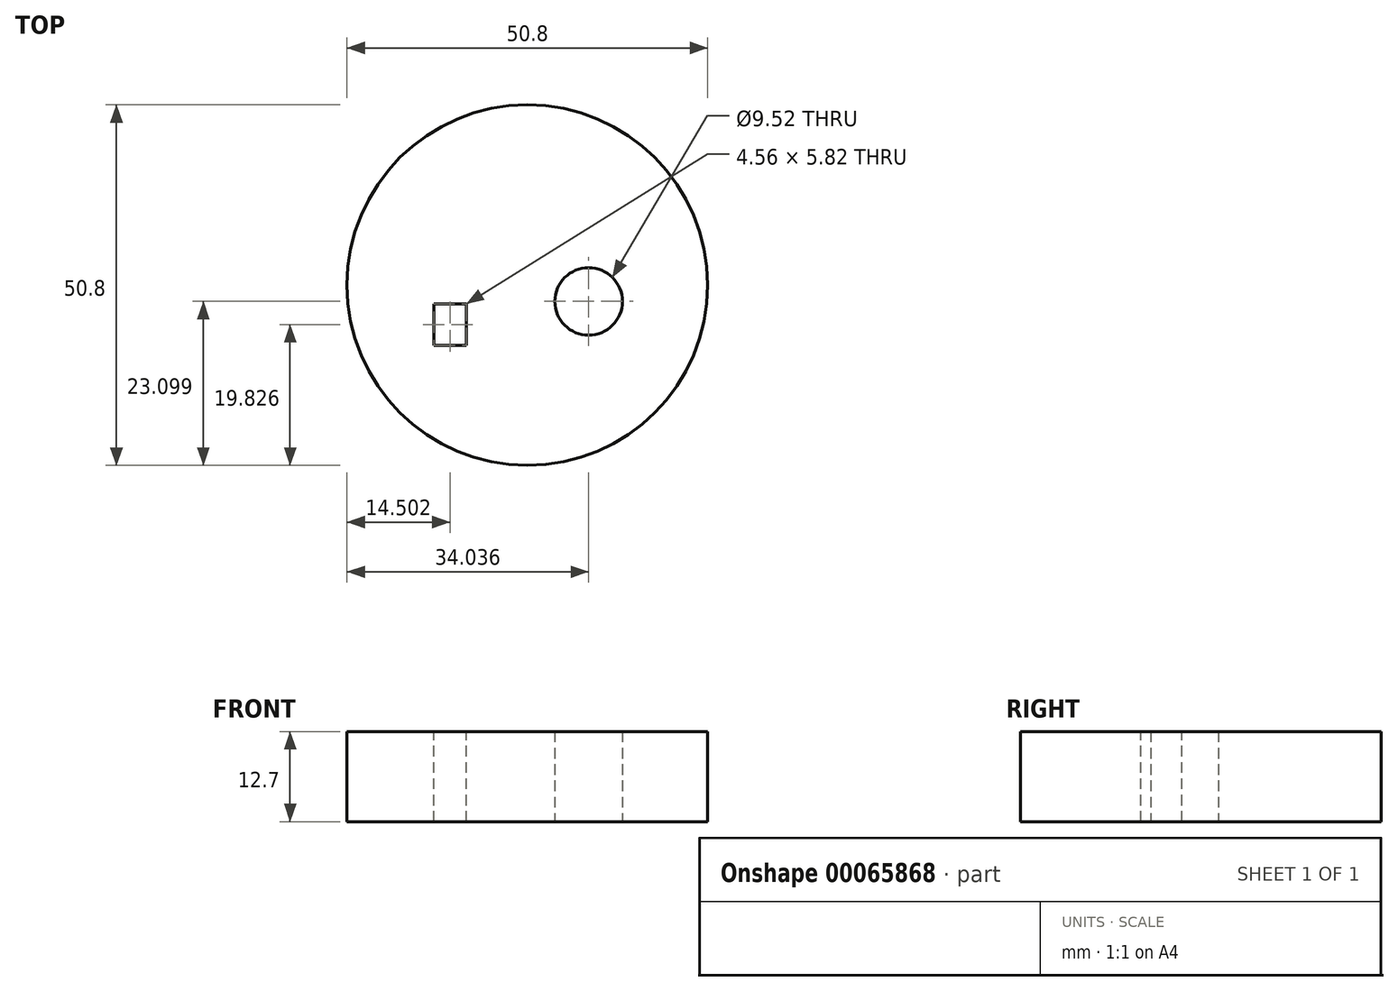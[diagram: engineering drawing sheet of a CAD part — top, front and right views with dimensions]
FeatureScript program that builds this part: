
annotation { "Feature Type Name" : "Feature", "Feature Type Description" : "" }
export const myFeature = defineFeature(function(context is Context, id is Id, definition is map)
    precondition{}
    {
        {
            var Q0;
            Q0=qCreatedBy(makeId("Top.planeOp"),FACE);
            var sketch = newSketch(context, id + "F0", { "sketchPlane" : qUnion([Q0])});
            skCircle(sketch, "E0", {"center": v(0, 0) * mm, "radius": 25.4 * mm});
            skSolve(sketch);
        }
        {
            var Q0;
            Q0 = qSketchRegion(id + "F0", true);
            extrude(context, id + "F1", {"entities" : qUnion([Q0]), "depth" : 12.7 * mm});
        }
        {
            var Q0;
            Q0=makeQuery(id+"F1.opExtrude","CAP_FACE",FACE,{"disambiguationData":[OSD([sQuery(id+"F0.wireOp",EDGE,"E0")])],"isStart":false});
            var sketch = newSketch(context, id + "F2", { "sketchPlane" : qUnion([Q0])});
            skLineSegment(sketch, "E1.bottom", {"start": v(-13.18, -8.48) * mm, "end": v(-8.62, -8.48) * mm});
            skLineSegment(sketch, "E1.top", {"start": v(-13.18, -2.67) * mm, "end": v(-8.62, -2.67) * mm});
            skLineSegment(sketch, "E1.left", {"start": v(-13.18, -8.48) * mm, "end": v(-13.18, -2.67) * mm});
            skLineSegment(sketch, "E1.right", {"start": v(-8.62, -8.48) * mm, "end": v(-8.62, -2.67) * mm});
            skSolve(sketch);
        }
        {
            var Q0;
            Q0 = qSketchRegion(id + "F2", true);
            extrude(context, id + "F3", {"entities" : qUnion([Q0]), "operationType" : NewBodyOperationType.REMOVE, "endBound" : BoundingType.THROUGH_ALL, "oppositeDirection" : true, "depth" : 25.4 * mm});
        }
        {
            var Q0;
            Q0=makeQuery(id+"F1.opExtrude","CAP_FACE",FACE,{"disambiguationData":[OSD([sQuery(id+"F0.wireOp",EDGE,"E0")])],"isStart":true});
            var sketch = newSketch(context, id + "F4", { "sketchPlane" : qUnion([Q0])});
            skCircle(sketch, "E2", {"center": v(8.64, 2.3) * mm, "radius": 4.76 * mm});
            skSolve(sketch);
        }
        {
            var Q0;
            Q0=makeQuery(id+"F4.imprint","IMPRINT",FACE,{"disambiguationData":[TD([[makeQuery(id+"F4.imprint","IMPRINT",EDGE,{"derivedFrom":sQuery(id+"F4.wireOp",EDGE,"E2")}),1.0]])]});
            var Q1;
            Q1=sQuery(id+"F4.wireOp",EDGE,"E2");
            extrude(context, id + "F5", {"entities" : qUnion([Q0]), "operationType" : NewBodyOperationType.REMOVE, "surfaceEntities" : qUnion([Q1]), "endBound" : BoundingType.THROUGH_ALL, "oppositeDirection" : true, "depth" : 25.4 * mm});
        }
    });
